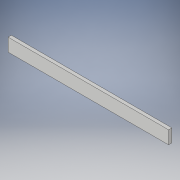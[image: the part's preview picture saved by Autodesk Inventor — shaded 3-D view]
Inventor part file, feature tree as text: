
AUTODESK INVENTOR PART (.ipt)
format: ipt  version: 2019 (Build 230136000, 136)  size: 93,184 bytes
history: native  units: mm
features: extrude x1, sketch x1
ambient origin geometry x8: Origin, YZ Plane, XZ Plane, XY Plane, X Axis, Y Axis, Z Axis, Center Point
bodies: Solid1 (feature_tree)
feature tree (2):
  extrude  "Extrusion1"  Depth=12.0mm
  sketch  "Sketch1"  dims[d0=148.627mm d1=12.0mm d2=3.1mm d3=0.0mm]
